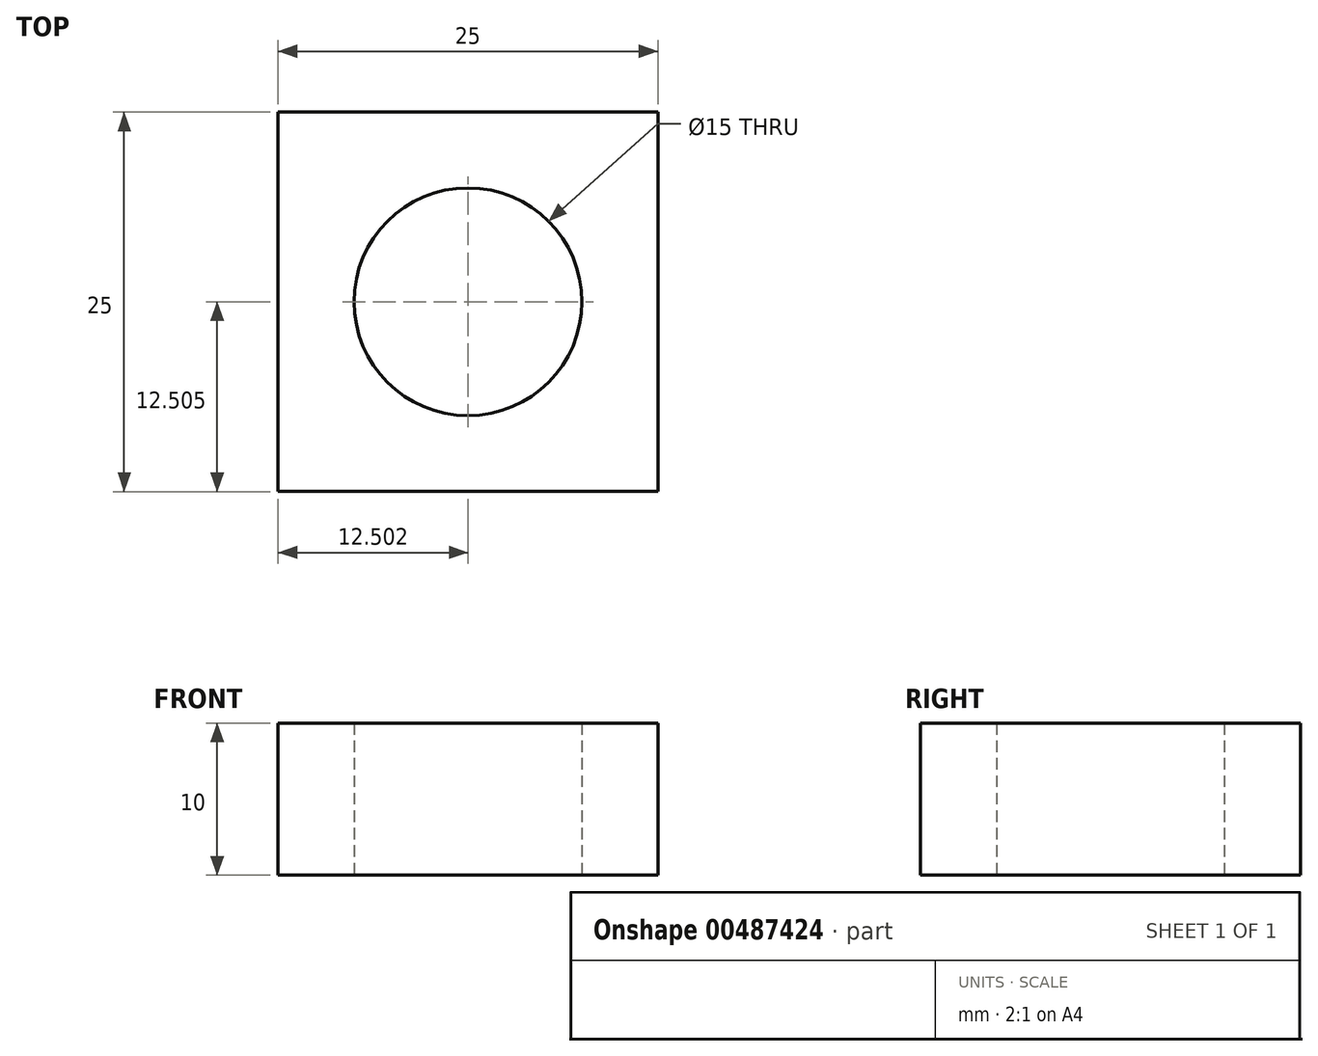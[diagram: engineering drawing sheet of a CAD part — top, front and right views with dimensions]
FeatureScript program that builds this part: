
annotation { "Feature Type Name" : "Feature", "Feature Type Description" : "" }
export const myFeature = defineFeature(function(context is Context, id is Id, definition is map)
    precondition{}
    {
        {
            var Q0;
            Q0=qCreatedBy(makeId("Top.planeOp"),FACE);
            var sketch = newSketch(context, id + "F0", { "sketchPlane" : qUnion([Q0])});
            skLineSegment(sketch, "E0.bottom", {"start": v(-12.97, 11.58) * mm, "end": v(12.03, 11.58) * mm});
            skLineSegment(sketch, "E0.top", {"start": v(-12.97, -13.42) * mm, "end": v(12.03, -13.42) * mm});
            skLineSegment(sketch, "E0.left", {"start": v(-12.97, 11.58) * mm, "end": v(-12.97, -13.42) * mm});
            skLineSegment(sketch, "E0.right", {"start": v(12.03, 11.58) * mm, "end": v(12.03, -13.42) * mm});
            skCircle(sketch, "E1", {"center": v(-0.47, -0.92) * mm, "radius": 7.5 * mm});
            skSolve(sketch);
        }
        {
            var Q0;
            Q0=makeQuery(id+"F0.imprint","IMPRINT",FACE,{"disambiguationData":[TD([[makeQuery(id+"F0.imprint","IMPRINT",EDGE,{"derivedFrom":sQuery(id+"F0.wireOp",EDGE,"E0.bottom")}),-1.0]])]});
            extrude(context, id + "F1", {"entities" : qUnion([Q0]), "depth" : 10 * mm});
        }
    });
